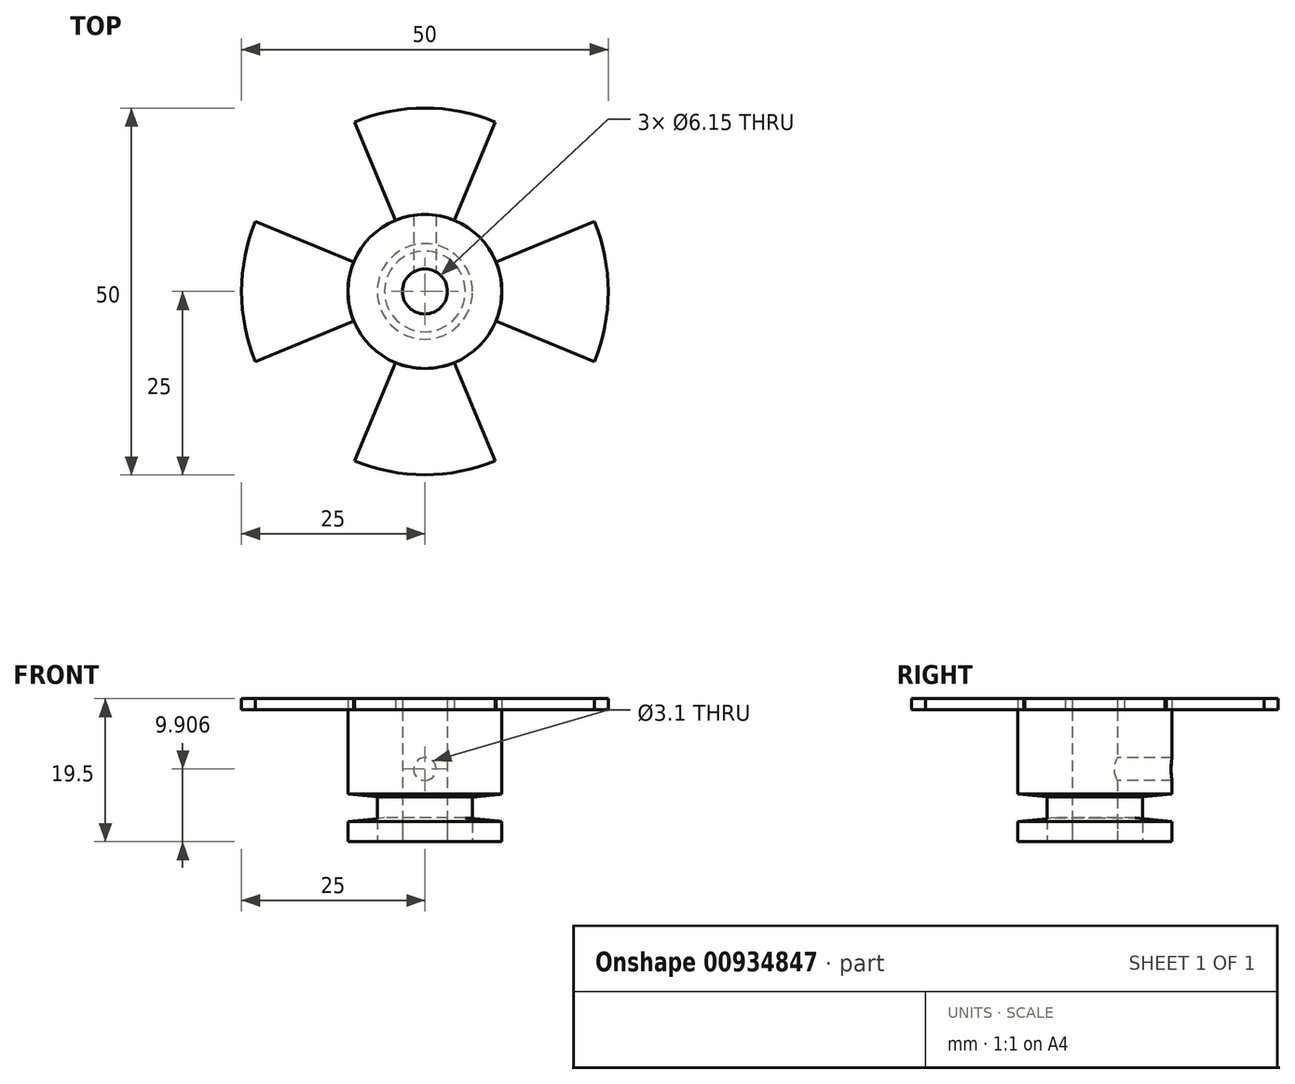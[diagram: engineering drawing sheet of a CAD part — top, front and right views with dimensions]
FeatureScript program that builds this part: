
annotation { "Feature Type Name" : "Feature", "Feature Type Description" : "" }
export const myFeature = defineFeature(function(context is Context, id is Id, definition is map)
    precondition{}
    {
        {
            var Q0;
            Q0=qCreatedBy(makeId("Top.planeOp"),FACE);
            var sketch = newSketch(context, id + "F0", { "sketchPlane" : qUnion([Q0])});
            skCircle(sketch, "E0", {"center": v(0, 0) * mm, "radius": 10.5 * mm});
            skCircle(sketch, "E1", {"center": v(0, 0) * mm, "radius": 3.08 * mm});
            skCircle(sketch, "E2", {"center": v(0, 0) * mm, "radius": 6.5 * mm});
            skSolve(sketch);
        }
        {
            var Q0;
            Q0=makeQuery(id+"F0.imprint","IMPRINT",FACE,{"disambiguationData":[TD([[makeQuery(id+"F0.imprint","IMPRINT",EDGE,{"derivedFrom":sQuery(id+"F0.wireOp",EDGE,"E1")}),-1.0]])]});
            var Q1;
            Q1=makeQuery(id+"F0.imprint","IMPRINT",FACE,{"disambiguationData":[TD([[makeQuery(id+"F0.imprint","IMPRINT",EDGE,{"derivedFrom":sQuery(id+"F0.wireOp",EDGE,"E0")}),1.0]])]});
            extrude(context, id + "F1", {"entities" : qUnion([Q0, Q1]), "depth" : 3.25 * mm, "offsetDistance" : 25 * mm});
        }
        {
            var Q0;
            Q0=makeQuery(id+"F0.imprint","IMPRINT",FACE,{"disambiguationData":[TD([[makeQuery(id+"F0.imprint","IMPRINT",EDGE,{"derivedFrom":sQuery(id+"F0.wireOp",EDGE,"E1")}),-1.0]])]});
            extrude(context, id + "F2", {"entities" : qUnion([Q0]), "depth" : 6 * mm, "offsetDistance" : 25 * mm});
        }
        {
            var Q0;
            Q0=makeQuery(id+"F2.opExtrude","CAP_FACE",FACE,{"disambiguationData":[OSD([sQuery(id+"F0.wireOp",EDGE,"E1"),sQuery(id+"F0.wireOp",EDGE,"E2")])],"isStart":false});
            var sketch = newSketch(context, id + "F3", { "sketchPlane" : qUnion([Q0])});
            skCircle(sketch, "E3.0", {"center": v(0, 0) * mm, "radius": 10.5 * mm});
            skSolve(sketch);
        }
        {
            var Q0;
            Q0=makeQuery(id+"F3.imprint","IMPRINT",FACE,{"disambiguationData":[TD([[makeQuery(id+"F3.imprint","IMPRINT",EDGE,{"derivedFrom":sQuery(id+"F3.wireOp",EDGE,"E3.0")}),1.0]])]});
            var Q1;
            Q1=makeQuery(id+"F3.imprint","IMPRINT",FACE,{"disambiguationData":[TD([[makeQuery(id+"F3.imprint","IMPRINT",EDGE,{"derivedFrom":makeQuery(id+"F2.opExtrude","CAP_EDGE",EDGE,{"disambiguationData":[OSD([sQuery(id+"F0.wireOp",EDGE,"E1")])],"isStart":false})}),-1.0]])]});
            extrude(context, id + "F4", {"entities" : qUnion([Q0, Q1]), "depth" : 12 * mm, "offsetDistance" : 25 * mm});
        }
        {
            var Q0;
            Q0=makeQuery(id+"F4.opExtrude","CAP_FACE",FACE,{"disambiguationData":[OSD([sQuery(id+"F0.wireOp",EDGE,"E2"),sQuery(id+"F3.wireOp",EDGE,"E3.0")])],"isStart":false});
            var sketch = newSketch(context, id + "F5", { "sketchPlane" : qUnion([Q0])});
            skCircle(sketch, "E4", {"center": v(0, 0) * mm, "radius": 25 * mm});
            skLineSegment(sketch, "E5", {"start": v(-25, 0) * mm, "end": v(25, 0) * mm});
            skLineSegment(sketch, "E6", {"start": v(0, -25) * mm, "end": v(0, 25) * mm});
            skLineSegment(sketch, "E7", {"start": v(17.68, -17.68) * mm, "end": v(-17.68, 17.68) * mm});
            skLineSegment(sketch, "E8.MirrorCS", {"start": v(17.68, 17.68) * mm, "end": v(-17.68, -17.68) * mm});
            skLineSegment(sketch, "E9", {"start": v(-9.57, -23.1) * mm, "end": v(9.57, 23.1) * mm});
            skLineSegment(sketch, "E10.MirrorCS", {"start": v(-9.57, 23.1) * mm, "end": v(9.57, -23.1) * mm});
            skLineSegment(sketch, "E11.MirrorCS", {"start": v(-23.1, 9.57) * mm, "end": v(23.1, -9.57) * mm});
            skLineSegment(sketch, "E12.MirrorCS", {"start": v(-23.1, -9.57) * mm, "end": v(23.1, 9.57) * mm});
            skSolve(sketch);
        }
        {
            var Q0;
            {var subQ0=sQuery(id+"F5.wireOp",EDGE,"E5");var subQ1=sQuery(id+"F5.wireOp",EDGE,"E4");var subQ2=makeQuery(id+"F5.imprint","INTERSECT",VERTEX,{"disambiguationData":[OD(1.0)],"derivedFrom":[subQ1,subQ0]});Q0=makeQuery(id+"F5.imprint","IMPRINT",FACE,{"disambiguationData":[TD([[makeQuery(id+"F5.imprint","IMPRINT",EDGE,{"disambiguationData":[TD([[subQ2,1.0]])],"derivedFrom":subQ1}),1.0]])]});}
            var Q1;
            {var subQ0=sQuery(id+"F5.wireOp",EDGE,"E5");var subQ1=sQuery(id+"F5.wireOp",EDGE,"E4");var subQ2=makeQuery(id+"F5.imprint","INTERSECT",VERTEX,{"disambiguationData":[OD(1.0)],"derivedFrom":[subQ1,subQ0]});Q1=makeQuery(id+"F5.imprint","IMPRINT",FACE,{"disambiguationData":[TD([[makeQuery(id+"F5.imprint","IMPRINT",EDGE,{"disambiguationData":[TD([[subQ2,-1.0]])],"derivedFrom":subQ1}),1.0]])]});}
            var Q2;
            {var subQ0=sQuery(id+"F5.wireOp",EDGE,"E6");var subQ1=sQuery(id+"F5.wireOp",EDGE,"E4");var subQ2=makeQuery(id+"F5.imprint","INTERSECT",VERTEX,{"disambiguationData":[OD(1.0)],"derivedFrom":[subQ1,subQ0]});Q2=makeQuery(id+"F5.imprint","IMPRINT",FACE,{"disambiguationData":[TD([[makeQuery(id+"F5.imprint","IMPRINT",EDGE,{"disambiguationData":[TD([[subQ2,1.0]])],"derivedFrom":subQ1}),1.0]])]});}
            var Q3;
            {var subQ0=sQuery(id+"F5.wireOp",EDGE,"E6");var subQ1=sQuery(id+"F5.wireOp",EDGE,"E4");var subQ2=makeQuery(id+"F5.imprint","INTERSECT",VERTEX,{"disambiguationData":[OD(1.0)],"derivedFrom":[subQ1,subQ0]});Q3=makeQuery(id+"F5.imprint","IMPRINT",FACE,{"disambiguationData":[TD([[makeQuery(id+"F5.imprint","IMPRINT",EDGE,{"disambiguationData":[TD([[subQ2,-1.0]])],"derivedFrom":subQ1}),1.0]])]});}
            var Q4;
            {var subQ0=sQuery(id+"F5.wireOp",EDGE,"E5");var subQ1=sQuery(id+"F5.wireOp",EDGE,"E4");var subQ2=makeQuery(id+"F5.imprint","INTERSECT",VERTEX,{"disambiguationData":[OD(0.0)],"derivedFrom":[subQ1,subQ0]});Q4=makeQuery(id+"F5.imprint","IMPRINT",FACE,{"disambiguationData":[TD([[makeQuery(id+"F5.imprint","IMPRINT",EDGE,{"disambiguationData":[TD([[subQ2,1.0]])],"derivedFrom":subQ1}),1.0]])]});}
            var Q5;
            {var subQ0=sQuery(id+"F5.wireOp",EDGE,"E5");var subQ1=sQuery(id+"F5.wireOp",EDGE,"E4");var subQ2=makeQuery(id+"F5.imprint","INTERSECT",VERTEX,{"disambiguationData":[OD(0.0)],"derivedFrom":[subQ1,subQ0]});Q5=makeQuery(id+"F5.imprint","IMPRINT",FACE,{"disambiguationData":[TD([[makeQuery(id+"F5.imprint","IMPRINT",EDGE,{"disambiguationData":[TD([[subQ2,-1.0]])],"derivedFrom":subQ1}),1.0]])]});}
            var Q6;
            {var subQ0=sQuery(id+"F5.wireOp",EDGE,"E6");var subQ1=sQuery(id+"F5.wireOp",EDGE,"E4");var subQ2=makeQuery(id+"F5.imprint","INTERSECT",VERTEX,{"disambiguationData":[OD(0.0)],"derivedFrom":[subQ1,subQ0]});Q6=makeQuery(id+"F5.imprint","IMPRINT",FACE,{"disambiguationData":[TD([[makeQuery(id+"F5.imprint","IMPRINT",EDGE,{"disambiguationData":[TD([[subQ2,1.0]])],"derivedFrom":subQ1}),1.0]])]});}
            var Q7;
            {var subQ0=sQuery(id+"F5.wireOp",EDGE,"E6");var subQ1=sQuery(id+"F5.wireOp",EDGE,"E4");var subQ2=makeQuery(id+"F5.imprint","INTERSECT",VERTEX,{"disambiguationData":[OD(0.0)],"derivedFrom":[subQ1,subQ0]});Q7=makeQuery(id+"F5.imprint","IMPRINT",FACE,{"disambiguationData":[TD([[makeQuery(id+"F5.imprint","IMPRINT",EDGE,{"disambiguationData":[TD([[subQ2,-1.0]])],"derivedFrom":subQ1}),1.0]])]});}
            extrude(context, id + "F6", {"entities" : qUnion([Q0, Q1, Q2, Q3, Q4, Q5, Q6, Q7]), "depth" : 1.5 * mm, "offsetDistance" : 25 * mm});
        }
        {
            var Q0;
            Q0=makeQuery(id+"F4.opExtrude","CAP_FACE",FACE,{"disambiguationData":[OSD([sQuery(id+"F0.wireOp",EDGE,"E2"),sQuery(id+"F3.wireOp",EDGE,"E3.0")])],"isStart":false});
            extrude(context, id + "F7", {"entities" : qUnion([Q0]), "depth" : 1.5 * mm, "offsetDistance" : 25 * mm});
        }
        {
            var Q0;
            Q0=qCreatedBy(makeId("Front.planeOp"),FACE);
            var sketch = newSketch(context, id + "F8", { "sketchPlane" : qUnion([Q0])});
            skLineSegment(sketch, "E13.0", {"start": v(-10.5, 0) * mm, "end": v(10.5, 0) * mm});
            skLineSegment(sketch, "E14.0", {"start": v(-9.57, 19.5) * mm, "end": v(9.57, 19.5) * mm});
            skCircle(sketch, "E15", {"center": v(0, 9.9) * mm, "radius": 1.55 * mm});
            skSolve(sketch);
        }
        {
            var Q0;
            Q0 = qSketchRegion(id + "F8", true);
            extrude(context, id + "F9", {"entities" : qUnion([Q0]), "operationType" : NewBodyOperationType.REMOVE, "oppositeDirection" : true, "depth" : 20 * mm, "offsetDistance" : 25 * mm});
        }
        {
            var Q0;
            Q0=makeQuery(id+"F1.opExtrude","CAP_EDGE",EDGE,{"disambiguationData":[OSD([sQuery(id+"F0.wireOp",EDGE,"E0")])],"isStart":false});
            chamfer(context, id + "F10", {"entities" : qUnion([Q0]), "chamferType" : ChamferType.TWO_OFFSETS, "width1" : 5 * mm, "oppositeDirection" : false, "width2" : .5 * mm, "tangentPropagation" : true});
        }
        {
            var Q0;
            Q0=makeQuery(id+"F4.opExtrude","CAP_EDGE",EDGE,{"disambiguationData":[OSD([sQuery(id+"F3.wireOp",EDGE,"E3.0")])],"isStart":true});
            chamfer(context, id + "F11", {"entities" : qUnion([Q0]), "chamferType" : ChamferType.TWO_OFFSETS, "width1" : .5 * mm, "oppositeDirection" : false, "width2" : 5 * mm, "tangentPropagation" : true});
        }
        {
            var Q0;
            Q0=makeQuery(id+"F2.opExtrude","CAP_FACE",FACE,{"disambiguationData":[OSD([sQuery(id+"F0.wireOp",EDGE,"E1"),sQuery(id+"F0.wireOp",EDGE,"E2")])],"isStart":false});
            extrude(context, id + "F12", {"entities" : qUnion([Q0]), "operationType" : NewBodyOperationType.ADD, "depth" : 1 * mm, "offsetDistance" : 25 * mm});
        }
    });
